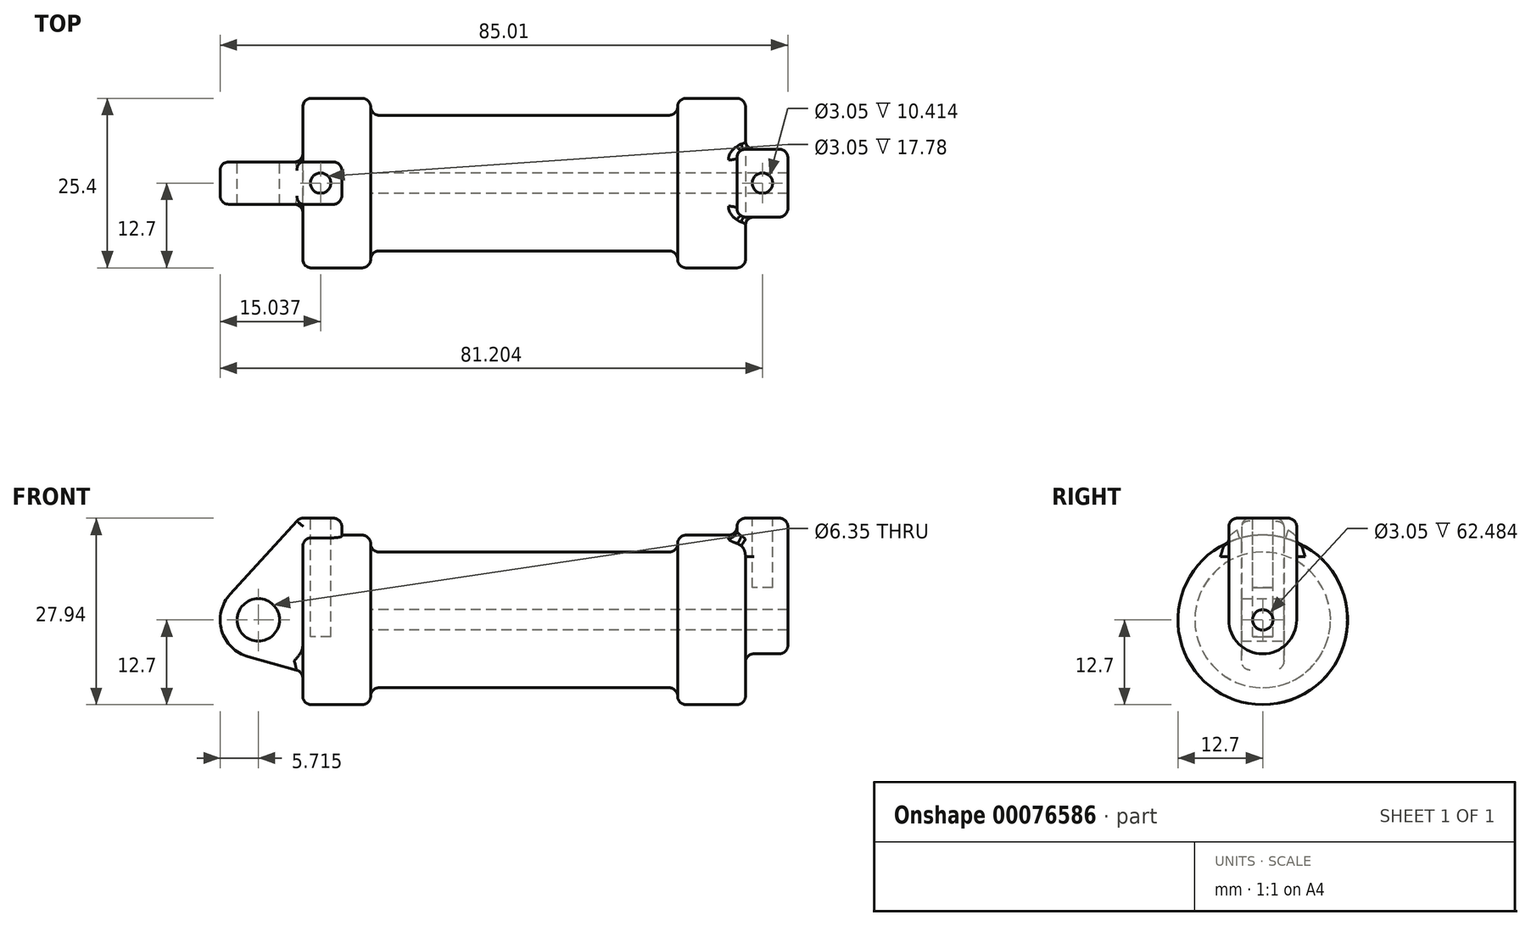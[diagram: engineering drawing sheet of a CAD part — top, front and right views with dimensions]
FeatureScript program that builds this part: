
annotation { "Feature Type Name" : "Feature", "Feature Type Description" : "" }
export const myFeature = defineFeature(function(context is Context, id is Id, definition is map)
    precondition{}
    {
        {
            var Q0;
            Q0=qCreatedBy(makeId("Front.planeOp"),FACE);
            var sketch = newSketch(context, id + "F0", { "sketchPlane" : qUnion([Q0])});
            skLineSegment(sketch, "E0", {"start": v(0, 0) * mm, "end": v(0, 12.7) * mm});
            skLineSegment(sketch, "E1", {"start": v(0, 12.7) * mm, "end": v(10.16, 12.7) * mm});
            skLineSegment(sketch, "E2", {"start": v(10.16, 12.7) * mm, "end": v(10.16, 10.16) * mm});
            skLineSegment(sketch, "E3", {"start": v(10.16, 10.16) * mm, "end": v(56.13, 10.16) * mm});
            skLineSegment(sketch, "E4", {"start": v(56.13, 10.16) * mm, "end": v(56.13, 12.7) * mm});
            skLineSegment(sketch, "E5", {"start": v(56.13, 12.7) * mm, "end": v(66.3, 12.7) * mm});
            skLineSegment(sketch, "E6", {"start": v(66.3, 12.7) * mm, "end": v(66.3, 0) * mm});
            skLineSegment(sketch, "E7", {"start": v(66.3, 0) * mm, "end": v(0, 0) * mm});
            skLineSegment(sketch, "E8", {"start": v(5.84, 15.24) * mm, "end": v(-0.5, 15.24) * mm});
            skLineSegment(sketch, "E9", {"start": v(-0.5, 15.24) * mm, "end": v(-10.88, 3.85) * mm});
            skLineSegment(sketch, "E10", {"start": v(0, 0) * mm, "end": v(-6.65, 0) * mm});
            skCircle(sketch, "E11", {"center": v(-6.65, 0) * mm, "radius": 5.72 * mm});
            skCircle(sketch, "E12", {"center": v(-6.65, 0) * mm, "radius": 3.18 * mm});
            skLineSegment(sketch, "E13", {"start": v(5.84, 15.24) * mm, "end": v(5.84, -9.4) * mm});
            skLineSegment(sketch, "E14", {"start": v(5.84, -9.4) * mm, "end": v(-8.18, -5.5) * mm});
            skSolve(sketch);
        }
        {
            var Q0;
            {var subQ0=sQuery(id+"F0.wireOp",EDGE,"E2");Q0=makeQuery(id+"F0.imprint","IMPRINT",FACE,{"disambiguationData":[TD([[makeQuery(id+"F0.imprint","IMPRINT",EDGE,{"derivedFrom":subQ0}),-1.0]])]});}
            var Q1;
            Q1=sQuery(id+"F0.wireOp",EDGE,"E7");
            revolve(context, id + "F1", {"entities" : qUnion([Q0]), "axis" : qUnion([Q1]), "revolveType" : RevolveType.FULL});
        }
        {
            var Q0;
            {var subQ3=sQuery(id+"F0.wireOp",EDGE,"E0");Q0=makeQuery(id+"F0.imprint","IMPRINT",FACE,{"disambiguationData":[TD([[makeQuery(id+"F0.imprint","IMPRINT",EDGE,{"derivedFrom":subQ3}),1.0]])]});}
            var Q1;
            {var subQ0=sQuery(id+"F0.wireOp",EDGE,"E14");Q1=makeQuery(id+"F0.imprint","IMPRINT",FACE,{"disambiguationData":[TD([[makeQuery(id+"F0.imprint","IMPRINT",EDGE,{"derivedFrom":subQ0}),-1.0]])]});}
            var Q2;
            {var subQ4=sQuery(id+"F0.wireOp",EDGE,"E12");Q2=makeQuery(id+"F0.imprint","IMPRINT",FACE,{"disambiguationData":[TD([[makeQuery(id+"F0.imprint","IMPRINT",EDGE,{"derivedFrom":subQ4}),-1.0]])]});}
            var Q3;
            {var subQ0=sQuery(id+"F0.wireOp",EDGE,"E0");Q3=makeQuery(id+"F0.imprint","IMPRINT",FACE,{"disambiguationData":[TD([[makeQuery(id+"F0.imprint","IMPRINT",EDGE,{"derivedFrom":subQ0}),-1.0]])]});}
            extrude(context, id + "F2", {"entities" : qUnion([Q0, Q1, Q2, Q3]), "operationType" : NewBodyOperationType.ADD, "endBound" : BoundingType.SYMMETRIC, "depth" : 6.35 * mm});
        }
        {
            var Q0;
            {var subQ0=sQuery(id+"F0.wireOp",EDGE,"E0");Q0=makeQuery(id+"F0.imprint","IMPRINT",FACE,{"disambiguationData":[TD([[makeQuery(id+"F0.imprint","IMPRINT",EDGE,{"derivedFrom":subQ0}),-1.0]])]});}
            var Q1;
            Q1=sQuery(id+"F0.wireOp",EDGE,"E7");
            revolve(context, id + "F3", {"operationType" : NewBodyOperationType.ADD, "entities" : qUnion([Q0]), "axis" : qUnion([Q1]), "revolveType" : RevolveType.FULL});
        }
        {
            var Q0;
            Q0=makeQuery(id+"F2.opExtrude","CAP_FACE",FACE,{"disambiguationData":[OSD([sQuery(id+"F0.wireOp",EDGE,"E8"),sQuery(id+"F0.wireOp",EDGE,"E9"),sQuery(id+"F0.wireOp",EDGE,"E11"),sQuery(id+"F0.wireOp",EDGE,"E13"),sQuery(id+"F0.wireOp",EDGE,"E14")])],"isStart":false});
            var sketch = newSketch(context, id + "F4", { "sketchPlane" : qUnion([Q0])});
            skCircle(sketch, "E15.0", {"center": v(-6.65, 0) * mm, "radius": 3.18 * mm});
            skSolve(sketch);
        }
        {
            var Q0;
            Q0 = qSketchRegion(id + "F4", true);
            extrude(context, id + "F5", {"entities" : qUnion([Q0]), "operationType" : NewBodyOperationType.REMOVE, "endBound" : BoundingType.THROUGH_ALL, "oppositeDirection" : true, "depth" : 25.4 * mm});
        }
        {
            var Q0;
            Q0=makeQuery(id+"F1.opRevolve","SWEPT_FACE",FACE,{"disambiguationData":[OSD([sQuery(id+"F0.wireOp",EDGE,"E6")])]});
            var sketch = newSketch(context, id + "F6", { "sketchPlane" : qUnion([Q0])});
            skLineSegment(sketch, "E16", {"start": v(0, 0) * mm, "end": v(0, 15.24) * mm, "construction": true});
            skCircle(sketch, "E17", {"center": v(0, 0) * mm, "radius": 1.52 * mm});
            skCircle(sketch, "E18", {"center": v(0, 0) * mm, "radius": 5.08 * mm});
            skLineSegment(sketch, "E19", {"start": v(0, 15.24) * mm, "end": v(5.08, 15.24) * mm});
            skLineSegment(sketch, "E20", {"start": v(5.08, 15.24) * mm, "end": v(5.08, 0) * mm});
            skLineSegment(sketch, "E21", {"start": v(0, 15.24) * mm, "end": v(-5.08, 15.24) * mm});
            skLineSegment(sketch, "E22", {"start": v(-5.08, 15.24) * mm, "end": v(-5.08, 0) * mm});
            skSolve(sketch);
        }
        {
            var Q0;
            Q0 = qSketchRegion(id + "F6", true);
            var Q1;
            Q1=makeQuery(id+"F6.imprint","IMPRINT",FACE,{"disambiguationData":[TD([[makeQuery(id+"F6.imprint","IMPRINT",EDGE,{"derivedFrom":sQuery(id+"F6.wireOp",EDGE,"E17")}),1.0]])]});
            extrude(context, id + "F7", {"entities" : qUnion([Q0, Q1]), "operationType" : NewBodyOperationType.ADD, "oppositeDirection" : true, "depth" : 1.27 * mm});
        }
        {
            var Q0;
            Q0 = qSketchRegion(id + "F6", true);
            extrude(context, id + "F8", {"entities" : qUnion([Q0]), "operationType" : NewBodyOperationType.ADD, "depth" : 6.35 * mm});
        }
        {
            var Q0;
            Q0=makeQuery(id+"F8.boolean.opBoolean","SPLIT",FACE,{"disambiguationData":[TD([makeQuery(id+"F8.opExtrude","SWEPT_FACE",FACE,{"disambiguationData":[OSD([sQuery(id+"F6.wireOp",EDGE,"E17")])]})])],"derivedFrom":makeQuery(id+"F7.boolean.opBoolean","MERGE",FACE,{"derivedFrom":[makeQuery(id+"F1.opRevolve","SWEPT_FACE",FACE,{"disambiguationData":[OSD([sQuery(id+"F0.wireOp",EDGE,"E6")])]}),makeQuery(id+"F7.opExtrude","CAP_FACE",FACE,{"disambiguationData":[OSD([sQuery(id+"F6.wireOp",EDGE,"E18"),sQuery(id+"F6.wireOp",EDGE,"E19"),sQuery(id+"F6.wireOp",EDGE,"E20"),sQuery(id+"F6.wireOp",EDGE,"E21"),sQuery(id+"F6.wireOp",EDGE,"E22")])],"isStart":true})]})});
            var Q1;
            Q1=makeQuery(id+"F1.opRevolve","SWEPT_FACE",FACE,{"disambiguationData":[OSD([sQuery(id+"F0.wireOp",EDGE,"E2")])]});
            var Q2;
            Q2=makeQuery(id+"F1.opRevolve","SWEPT_BODY",BODY,{"disambiguationData":[OSD([sQuery(id+"F0.wireOp",EDGE,"E1"),sQuery(id+"F0.wireOp",EDGE,"E2"),sQuery(id+"F0.wireOp",EDGE,"E3"),sQuery(id+"F0.wireOp",EDGE,"E4"),sQuery(id+"F0.wireOp",EDGE,"E5"),sQuery(id+"F0.wireOp",EDGE,"E6"),sQuery(id+"F0.wireOp",EDGE,"E7"),sQuery(id+"F0.wireOp",EDGE,"E13")])]});
            extrude(context, id + "F9", {"entities" : qUnion([Q0]), "operationType" : NewBodyOperationType.REMOVE, "endBound" : BoundingType.UP_TO_SURFACE, "oppositeDirection" : true, "endBoundEntityFace" : qUnion([Q1]), "endBoundEntityBody" : qUnion([Q2]), "depth" : 1.27 * mm});
        }
        {
            var Q0;
            {var subQ0=sQuery(id+"F6.wireOp",EDGE,"E21");var subQ1=sQuery(id+"F6.wireOp",EDGE,"E19");Q0=makeQuery(id+"F8.boolean.opBoolean","MERGE",FACE,{"derivedFrom":[makeQuery(id+"F7.opExtrude","SWEPT_FACE",FACE,{"disambiguationData":[OSD([subQ1,subQ0])]}),makeQuery(id+"F8.opExtrude","SWEPT_FACE",FACE,{"disambiguationData":[OSD([subQ1,subQ0])]})]});}
            var sketch = newSketch(context, id + "F10", { "sketchPlane" : qUnion([Q0])});
            skLineSegment(sketch, "E23", {"start": v(68.83, 5.08) * mm, "end": v(68.83, -5.08) * mm, "construction": true});
            skLineSegment(sketch, "E24", {"start": v(72.64, 0) * mm, "end": v(65.02, 0) * mm, "construction": true});
            skCircle(sketch, "E25", {"center": v(68.83, 0) * mm, "radius": 1.52 * mm});
            skSolve(sketch);
        }
        {
            var Q0;
            Q0=makeQuery(id+"F10.imprint","IMPRINT",FACE,{"disambiguationData":[TD([[makeQuery(id+"F10.imprint","IMPRINT",EDGE,{"derivedFrom":sQuery(id+"F10.wireOp",EDGE,"E25")}),1.0]])]});
            extrude(context, id + "F11", {"entities" : qUnion([Q0]), "operationType" : NewBodyOperationType.REMOVE, "oppositeDirection" : true, "depth" : 10.4 * mm});
        }
        {
            var Q0;
            Q0=makeQuery(id+"F2.opExtrude","SWEPT_FACE",FACE,{"disambiguationData":[OSD([sQuery(id+"F0.wireOp",EDGE,"E8")])]});
            var sketch = newSketch(context, id + "F12", { "sketchPlane" : qUnion([Q0])});
            skLineSegment(sketch, "E26", {"start": v(2.67, 3.18) * mm, "end": v(2.67, -3.18) * mm, "construction": true});
            skLineSegment(sketch, "E27", {"start": v(5.84, 0) * mm, "end": v(-0.5, 0) * mm, "construction": true});
            skCircle(sketch, "E28", {"center": v(2.67, 0) * mm, "radius": 1.52 * mm});
            skSolve(sketch);
        }
        {
            var Q0;
            Q0=makeQuery(id+"F12.imprint","IMPRINT",FACE,{"disambiguationData":[TD([[makeQuery(id+"F12.imprint","IMPRINT",EDGE,{"derivedFrom":sQuery(id+"F12.wireOp",EDGE,"E28")}),1.0]])]});
            var Q1;
            Q1=sQuery(id+"F12.wireOp",EDGE,"E28");
            extrude(context, id + "F13", {"entities" : qUnion([Q0]), "operationType" : NewBodyOperationType.REMOVE, "surfaceEntities" : qUnion([Q1]), "oppositeDirection" : true, "depth" : 17.78 * mm});
        }
        {
            var Q0;
            Q0=makeQuery(id+"F1.opRevolve","SWEPT_FACE",FACE,{"disambiguationData":[OSD([sQuery(id+"F0.wireOp",EDGE,"E3")])]});
            var Q1;
            Q1=makeQuery(id+"F1.opRevolve","SWEPT_EDGE",EDGE,{"disambiguationData":[OSD([sQuery(id+"F0.wireOp",EDGE,"E3"),sQuery(id+"F0.wireOp",EDGE,"E4")])]});
            fillet(context, id + "F14", {"entities" : qUnion([Q0, Q1]), "radius" : 1.27 * mm, "tangentPropagation" : true, "allowEdgeOverflow" : false});
        }
        {
            var Q0;
            Q0=makeQuery(id+"F1.opRevolve","SWEPT_EDGE",EDGE,{"disambiguationData":[OSD([sQuery(id+"F0.wireOp",EDGE,"E1"),sQuery(id+"F0.wireOp",EDGE,"E2")])]});
            var Q1;
            Q1=makeQuery(id+"F3.opRevolve","SWEPT_EDGE",EDGE,{"disambiguationData":[OSD([sQuery(id+"F0.wireOp",EDGE,"E0"),sQuery(id+"F0.wireOp",EDGE,"E1")])]});
            fillet(context, id + "F15", {"entities" : qUnion([Q0, Q1]), "radius" : 1.27 * mm, "tangentPropagation" : true, "allowEdgeOverflow" : false});
        }
        {
            var Q0;
            Q0=makeQuery(id+"F2.opExtrude","CAP_EDGE",EDGE,{"disambiguationData":[OSD([sQuery(id+"F0.wireOp",EDGE,"E9")])],"isStart":false});
            var Q1;
            Q1=makeQuery(id+"F2.opExtrude","CAP_EDGE",EDGE,{"disambiguationData":[OSD([sQuery(id+"F0.wireOp",EDGE,"E9")])],"isStart":true});
            var Q2;
            Q2=makeQuery(id+"F3.boolean.opBoolean","INTERSECT",EDGE,{"derivedFrom":[makeQuery(id+"F2.opExtrude","SWEPT_FACE",FACE,{"disambiguationData":[OSD([sQuery(id+"F0.wireOp",EDGE,"E14")])]}),makeQuery(id+"F3.opRevolve","SWEPT_FACE",FACE,{"disambiguationData":[OSD([sQuery(id+"F0.wireOp",EDGE,"E0")])]})]});
            var Q3;
            {var subQ0=sQuery(id+"F0.wireOp",EDGE,"E13");var subQ1=sQuery(id+"F0.wireOp",EDGE,"E8");Q3=makeQuery(id+"F2.boolean.opBoolean","SPLIT",EDGE,{"disambiguationData":[TD([makeQuery(id+"F2.opExtrude","SWEPT_FACE",FACE,{"disambiguationData":[OSD([subQ1])]})])],"derivedFrom":makeQuery(id+"F2.opExtrude","CAP_EDGE",EDGE,{"disambiguationData":[OSD([subQ0])],"isStart":true})});}
            var Q4;
            {var subQ0=sQuery(id+"F0.wireOp",EDGE,"E8");var subQ1=sQuery(id+"F0.wireOp",EDGE,"E13");Q4=makeQuery(id+"F2.boolean.opBoolean","SPLIT",EDGE,{"disambiguationData":[TD([makeQuery(id+"F2.opExtrude","SWEPT_FACE",FACE,{"disambiguationData":[OSD([subQ0])]})])],"derivedFrom":makeQuery(id+"F2.opExtrude","CAP_EDGE",EDGE,{"disambiguationData":[OSD([subQ1])],"isStart":false})});}
            var Q5;
            Q5=makeQuery(id+"F2.opExtrude","SWEPT_EDGE",EDGE,{"disambiguationData":[OSD([sQuery(id+"F0.wireOp",EDGE,"E8"),sQuery(id+"F0.wireOp",EDGE,"E13")])]});
            var Q6;
            Q6=makeQuery(id+"F2.opExtrude","CAP_EDGE",EDGE,{"disambiguationData":[OSD([sQuery(id+"F0.wireOp",EDGE,"E8")])],"isStart":true});
            var Q7;
            Q7=makeQuery(id+"F2.opExtrude","CAP_EDGE",EDGE,{"disambiguationData":[OSD([sQuery(id+"F0.wireOp",EDGE,"E8")])],"isStart":false});
            fillet(context, id + "F16", {"entities" : qUnion([Q0, Q1, Q2, Q3, Q4, Q5, Q6, Q7]), "radius" : 1.27 * mm, "tangentPropagation" : true, "allowEdgeOverflow" : false});
        }
        {
            var Q0;
            Q0=makeQuery(id+"F2.opExtrude","SWEPT_EDGE",EDGE,{"disambiguationData":[OSD([sQuery(id+"F0.wireOp",EDGE,"E8"),sQuery(id+"F0.wireOp",EDGE,"E9")])]});
            fillet(context, id + "F17", {"entities" : qUnion([Q0]), "radius" : 1.27 * mm, "tangentPropagation" : true, "allowEdgeOverflow" : false});
        }
        {
            var Q0;
            Q0=makeQuery(id+"F8.opExtrude","CAP_EDGE",EDGE,{"disambiguationData":[OSD([sQuery(id+"F6.wireOp",EDGE,"E22")])],"isStart":false});
            var Q1;
            {var subQ0=sQuery(id+"F6.wireOp",EDGE,"E22");var subQ1=sQuery(id+"F6.wireOp",EDGE,"E21");Q1=makeQuery(id+"F8.boolean.opBoolean","MERGE",EDGE,{"derivedFrom":[makeQuery(id+"F7.opExtrude","SWEPT_EDGE",EDGE,{"disambiguationData":[OSD([subQ1,subQ0])]}),makeQuery(id+"F8.opExtrude","SWEPT_EDGE",EDGE,{"disambiguationData":[OSD([subQ1,subQ0])]})]});}
            var Q2;
            Q2=makeQuery(id+"F8.opExtrude","CAP_EDGE",EDGE,{"disambiguationData":[OSD([sQuery(id+"F6.wireOp",EDGE,"E19"),sQuery(id+"F6.wireOp",EDGE,"E21")])],"isStart":false});
            var Q3;
            Q3=makeQuery(id+"F7.opExtrude","CAP_EDGE",EDGE,{"disambiguationData":[OSD([sQuery(id+"F6.wireOp",EDGE,"E19"),sQuery(id+"F6.wireOp",EDGE,"E21")])],"isStart":false});
            var Q4;
            {var subQ0=sQuery(id+"F6.wireOp",EDGE,"E20");var subQ1=sQuery(id+"F6.wireOp",EDGE,"E19");Q4=makeQuery(id+"F8.boolean.opBoolean","MERGE",EDGE,{"derivedFrom":[makeQuery(id+"F7.opExtrude","SWEPT_EDGE",EDGE,{"disambiguationData":[OSD([subQ1,subQ0])]}),makeQuery(id+"F8.opExtrude","SWEPT_EDGE",EDGE,{"disambiguationData":[OSD([subQ1,subQ0])]})]});}
            var Q5;
            Q5=makeQuery(id+"F7.opExtrude","CAP_EDGE",EDGE,{"disambiguationData":[OSD([sQuery(id+"F6.wireOp",EDGE,"E22")])],"isStart":false});
            var Q6;
            Q6=makeQuery(id+"F7.opExtrude","CAP_EDGE",EDGE,{"disambiguationData":[OSD([sQuery(id+"F6.wireOp",EDGE,"E20")])],"isStart":false});
            fillet(context, id + "F18", {"entities" : qUnion([Q0, Q1, Q2, Q3, Q4, Q5, Q6]), "radius" : 1.27 * mm, "tangentPropagation" : true, "allowEdgeOverflow" : false});
        }
        {
            var Q0;
            Q0=makeQuery(id+"F1.opRevolve","SWEPT_EDGE",EDGE,{"disambiguationData":[OSD([sQuery(id+"F0.wireOp",EDGE,"E4"),sQuery(id+"F0.wireOp",EDGE,"E5")])]});
            fillet(context, id + "F19", {"entities" : qUnion([Q0]), "radius" : 1.27 * mm, "tangentPropagation" : true, "allowEdgeOverflow" : false});
        }
        {
            var Q0;
            Q0=makeQuery(id+"F1.opRevolve","SWEPT_EDGE",EDGE,{"disambiguationData":[OSD([sQuery(id+"F0.wireOp",EDGE,"E5"),sQuery(id+"F0.wireOp",EDGE,"E6")])]});
            fillet(context, id + "F20", {"entities" : qUnion([Q0]), "radius" : 1.27 * mm, "tangentPropagation" : true, "allowEdgeOverflow" : false});
        }
        {
            var Q0;
            Q0=makeQuery(id+"F8.opExtrude","CAP_EDGE",EDGE,{"disambiguationData":[OSD([sQuery(id+"F6.wireOp",EDGE,"E22")])],"isStart":true});
            var Q1;
            Q1=makeQuery(id+"F8.opExtrude","CAP_EDGE",EDGE,{"disambiguationData":[OSD([sQuery(id+"F6.wireOp",EDGE,"E18")])],"isStart":true});
            var Q2;
            Q2=makeQuery(id+"F8.opExtrude","CAP_EDGE",EDGE,{"disambiguationData":[OSD([sQuery(id+"F6.wireOp",EDGE,"E20")])],"isStart":true});
            var Q3;
            Q3=makeQuery(id+"F7.boolean.opBoolean","INTERSECT",EDGE,{"derivedFrom":[makeQuery(id+"F1.opRevolve","SWEPT_FACE",FACE,{"disambiguationData":[OSD([sQuery(id+"F0.wireOp",EDGE,"E5")])]}),makeQuery(id+"F7.opExtrude","CAP_FACE",FACE,{"disambiguationData":[OSD([sQuery(id+"F6.wireOp",EDGE,"E18"),sQuery(id+"F6.wireOp",EDGE,"E19"),sQuery(id+"F6.wireOp",EDGE,"E20"),sQuery(id+"F6.wireOp",EDGE,"E21"),sQuery(id+"F6.wireOp",EDGE,"E22")])],"isStart":false})]});
            fillet(context, id + "F21", {"entities" : qUnion([Q0, Q1, Q2, Q3]), "radius" : 1.27 * mm, "allowEdgeOverflow" : false});
        }
    });
